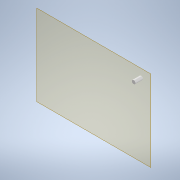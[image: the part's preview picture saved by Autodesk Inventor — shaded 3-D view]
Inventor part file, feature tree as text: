
AUTODESK INVENTOR PART (.ipt)
format: ipt  version: 2020 (Build 240168000, 168)  size: 93,696 bytes
history: native  units: in
note: dims shown in document units (in); Inventor stores cm internally (conversion verified against a paired STEP export)
features: other x2, plane x1, extrude x1, sketch x1, reference x1
ambient origin geometry x8: Origin, YZ Plane, XZ Plane, XY Plane, X Axis, Y Axis, Z Axis, Center Point
bodies: Solid1 (feature_tree)
feature tree (6):
  plane  "Work Plane1"
  extrude  "Extrusion1"  [1 undecoded]
  sketch  "Sketch1"  dims[d0=0.24in d1=0.0in]
  reference  "Reference1"
  other  "Assembly1"
  other  "Odroid-XU4 v1:1"
note: 1 required parameter value undecoded (feature->parameter linkage not recoverable at this tier; creation-order binding heuristic only, values carry confidence <= 0.55)
